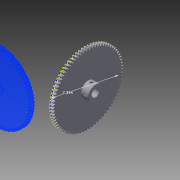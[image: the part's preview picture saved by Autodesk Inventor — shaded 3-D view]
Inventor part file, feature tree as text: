
AUTODESK INVENTOR PART (.ipt)
format: ipt  version: 2012 (Build 160160000, 160)  size: 2,364,928 bytes
history: native  units: in
note: dims shown in document units (in); Inventor stores cm internally (conversion verified against a paired STEP export)
features: other x4, sketch x1
ambient origin geometry x8: Origin, YZ Plane, XZ Plane, XY Plane, X Axis, Y Axis, Z Axis, Center Point
bodies: Solid1 (feature_tree), Solid2 (feature_tree)
feature tree (5):
  other  "s1066z-032s075-2.ipt"
  other  "69823::s1066z-032s075-2.ipt"
  other  "69823_1::s1066z-032s075-2.ipt"
  sketch  "Sketch1"  dims[d0=0.3937in]
  other  "TaggingFeature1"
